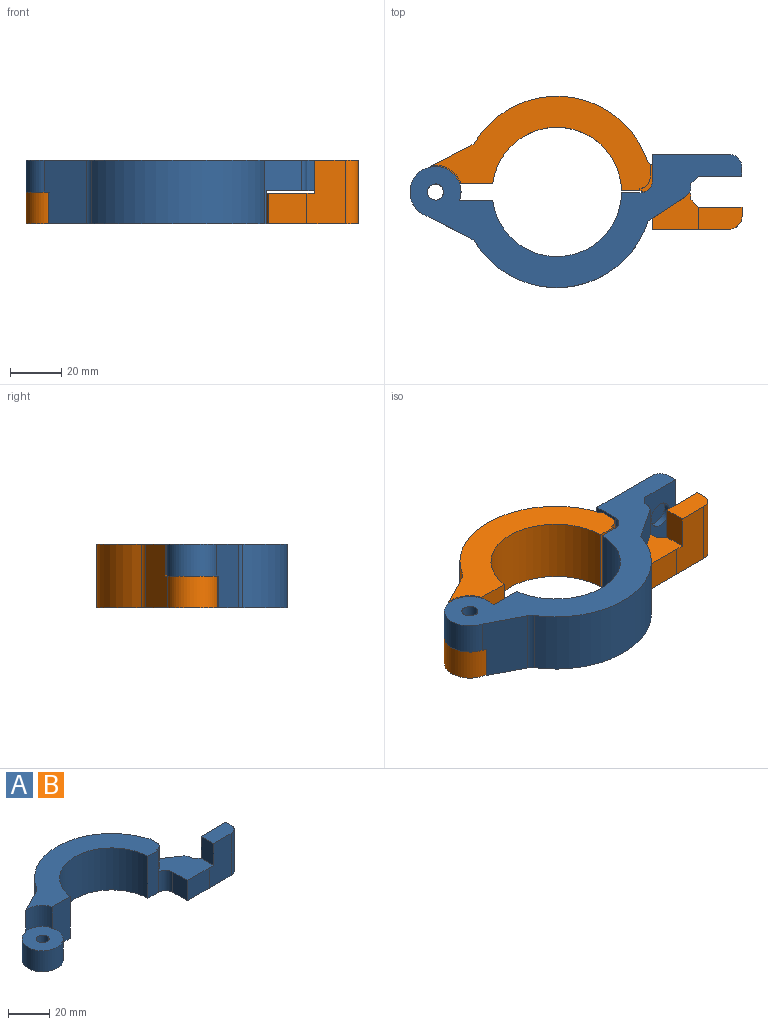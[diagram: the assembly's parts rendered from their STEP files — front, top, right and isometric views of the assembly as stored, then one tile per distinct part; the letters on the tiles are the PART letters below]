
ASSEMBLY  parts=2 mates=1
PART A: 31 faces, bbox 130x52x25 mm
  f0: plane 13x1mm, normal (1,0,0), area 13mm2, adj f5,f10,f23,f26
  f1: plane 12x0.79mm, normal (1,0,0), area 9.5mm2, adj f17,f18,f23,f25
  f2: plane 15x12mm, normal (0,-1,0), area 180mm2, adj f3,f11,f17,f23
  f3: plane 25x15mm, normal (0,-1,0), area 336mm2, adj f2,f16,f17,f22,f23,f30
  f4: plane 25x14.5mm, normal (0.55,0.84,0), area 219.6mm2, adj f5,f13,f17,f18,f21,f23
  f5: plane 85.18x37.05mm, normal (0,0,1), area 1215.7mm2, adj f0,f4,f6,f8,f10,f13,f14,f15
  f6: plane 25x16.6mm, normal (-0.46,0.89,0), area 444mm2, adj f5,f7,f14,f17,f19,f20
  f7: cylinder r=10mm len=20mm, axis (0,0,-1), area 596.9mm2, adj f6,f8,f17,f20
  f8: plane 25x12.98mm, normal (0,-1,0), area 317.8mm2, adj f5,f7,f15,f17,f19,f20
  f9: cylinder r=3.15mm len=12.5mm, axis (0,0,-1), area 247.4mm2, adj f17,f20
  f10: plane 25x7.15mm, normal (0,-1,0), area 178.8mm2, adj f0,f5,f15,f17,f23,f29
  f11: plane 12x10mm, normal (-1,0,0), area 120mm2, adj f2,f17,f23,f29
  f12: plane 25x3.5mm, normal (1,0,0), area 87.5mm2, adj f16,f17,f24,f30
  f13: cylinder r=37.5mm len=67.49mm, axis (0,0,-1), area 2130.5mm2, adj f4,f5,f14,f17
  f14: cylinder r=5mm len=25mm, axis (0,0,-1), area 66.8mm2, adj f5,f6,f13,f17
  f15: cylinder r=25.35mm len=50.47mm, axis (0,0,-1), area 1894.2mm2, adj f5,f8,f10,f17
  f16: plane 17x8.5mm, normal (0,0,1), area 139.1mm2, adj f3,f12,f22,f24,f30
  f17: plane 130x52.05mm, normal (0,0,-1), area 1995.2mm2, adj f1,f2,f3,f4,f6,f7,f8,f9
  f18: cylinder r=5mm len=12mm, axis (0,0,1), area 59.6mm2, adj f1,f4,f17,f23
  f19: cylinder r=10.5mm len=12.5mm, axis (0,0,1), area 177.7mm2, adj f5,f6,f8,f20
  f20: plane 20.5x20mm, normal (0,0,1), area 290.3mm2, adj f6,f7,f8,f9,f19
  f21: plane 13x5.43mm, normal (1,0,0), area 70.6mm2, adj f4,f5,f23,f26
  f22: plane 13x8.5mm, normal (-1,0,0), area 110.5mm2, adj f3,f16,f23,f24
  f23: plane 25.43x23mm, normal (0,0,1), area 350.1mm2, adj f0,f1,f2,f3,f4,f10,f11,f18
  f24: plane 25x17mm, normal (0,1,0), area 346.5mm2, adj f12,f16,f17,f22,f25,f27
  f25: plane 12x3mm, normal (0.71,0.71,0), area 50.9mm2, adj f1,f17,f23,f24
  f26: cylinder r=4mm len=13mm, axis (0,0,1), area 81.7mm2, adj f0,f5,f21,f23
  f27: cylinder r=5mm len=10mm, axis (0,1,0), area 78.5mm2, adj f24,f28
  f28: plane 10x10mm, normal (0,1,0), area 78.5mm2, adj f27
  f29: cylinder r=5mm len=12mm, axis (0,0,1), area 94.2mm2, adj f10,f11,f17,f23
  f30: cylinder r=5mm len=25mm, axis (0,0,-1), area 196.3mm2, adj f3,f12,f16,f17
PART B: same geometry as A
PLACE A rot(axis=(1,0,0),180deg) t=(14.03,10.78,35.82)mm
PLACE B t=(14.03,10.73,10.82)mm fixed
MATE revolute B.f19 <-> A.f9  axis (0,0,1) through (-33.47,10.73,23.32)mm
